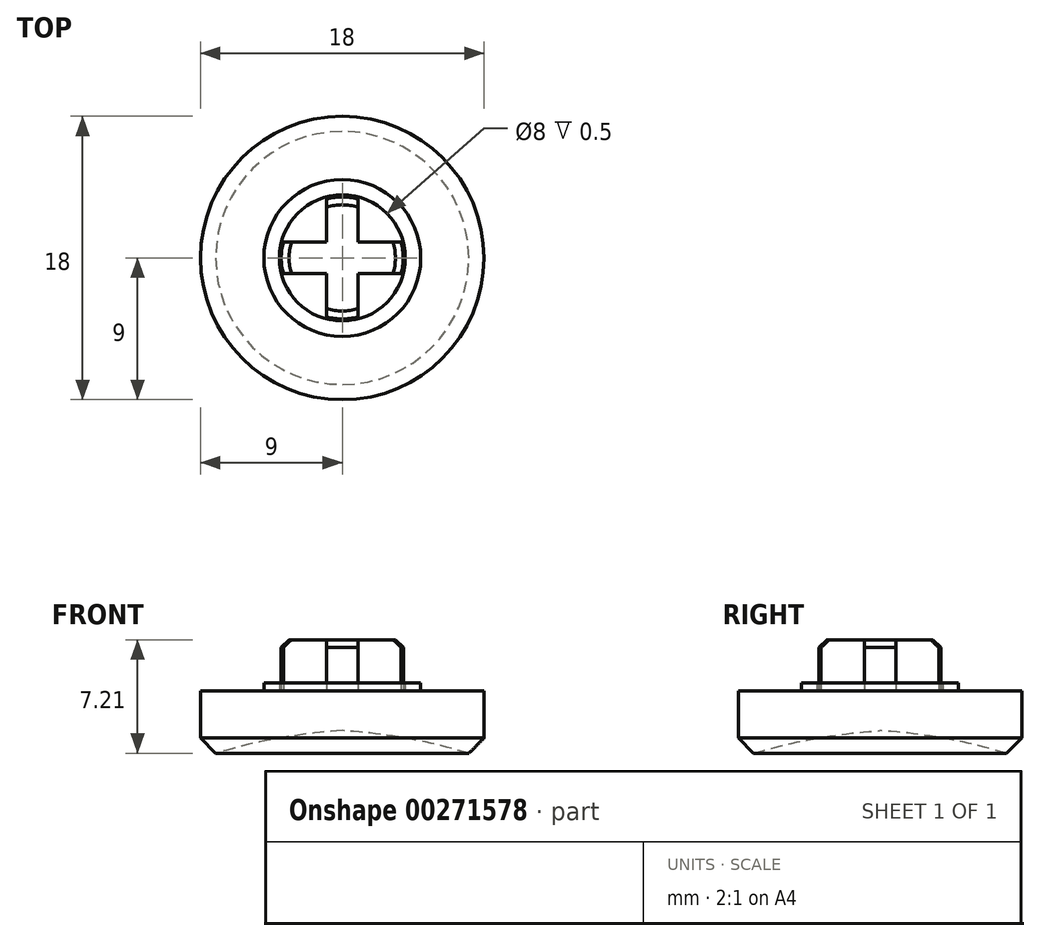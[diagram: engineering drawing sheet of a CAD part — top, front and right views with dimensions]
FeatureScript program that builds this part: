
annotation { "Feature Type Name" : "Feature", "Feature Type Description" : "" }
export const myFeature = defineFeature(function(context is Context, id is Id, definition is map)
    precondition{}
    {
        {
            var Q0;
            Q0=qCreatedBy(makeId("Top.planeOp"),FACE);
            var sketch = newSketch(context, id + "F0", { "sketchPlane" : qUnion([Q0])});
            skCircle(sketch, "E0", {"center": v(0, 0) * mm, "radius": 9 * mm});
            skLineSegment(sketch, "E1", {"start": v(-9.45, 0) * mm, "end": v(-9, 0) * mm});
            skLineSegment(sketch, "E2.left", {"start": v(-1, 3.74) * mm, "end": v(-1, 1) * mm});
            skLineSegment(sketch, "E2.right", {"start": v(1, 3.74) * mm, "end": v(1, 1) * mm});
            skLineSegment(sketch, "E3.bottom", {"start": v(-3.74, 1) * mm, "end": v(-1, 1) * mm});
            skLineSegment(sketch, "E3.top", {"start": v(-3.74, -1) * mm, "end": v(-1, -1) * mm});
            skCircle(sketch, "E4", {"center": v(0, 0) * mm, "radius": 3.88 * mm});
            skLineSegment(sketch, "E5.trimOffspring", {"start": v(1, 1) * mm, "end": v(3.74, 1) * mm});
            skLineSegment(sketch, "E6.trimOffspring", {"start": v(-1, -1) * mm, "end": v(-1, -3.74) * mm});
            skLineSegment(sketch, "E7.trimOffspring", {"start": v(1, -1) * mm, "end": v(1, -3.74) * mm});
            skLineSegment(sketch, "E8.trimOffspring", {"start": v(1, -1) * mm, "end": v(3.74, -1) * mm});
            skPoint(sketch, "E9.start.orphan", {"position": v(0, 9) * mm});
            skSolve(sketch);
        }
        {
            var Q0;
            Q0 = qSketchRegion(id + "F0", true);
            extrude(context, id + "F1", {"entities" : qUnion([Q0]), "depth" : 4 * mm});
        }
        {
            var Q0;
            Q0=makeQuery(id+"F1.opExtrude","CAP_FACE",FACE,{"disambiguationData":[OSD([sQuery(id+"F0.wireOp",EDGE,"E0")])],"isStart":false});
            var sketch = newSketch(context, id + "F2", { "sketchPlane" : qUnion([Q0])});
            skCircle(sketch, "E10", {"center": v(0, 0) * mm, "radius": 4 * mm});
            skCircle(sketch, "E11", {"center": v(0, 0) * mm, "radius": 4.98 * mm});
            skSolve(sketch);
        }
        {
            var Q0;
            {var subQ5=sQuery(id+"F0.wireOp",EDGE,"E2.left");Q0=makeQuery(id+"F0.imprint","IMPRINT",FACE,{"disambiguationData":[TD([[makeQuery(id+"F0.imprint","IMPRINT",EDGE,{"derivedFrom":subQ5}),1.0]])]});}
            extrude(context, id + "F3", {"entities" : qUnion([Q0]), "operationType" : NewBodyOperationType.ADD, "depth" : 7.25 * mm});
        }
        {
            var Q0;
            {var subQ0=sQuery(id+"F0.wireOp",EDGE,"E2.left");Q0=makeQuery(id+"F0.imprint","IMPRINT",FACE,{"disambiguationData":[TD([[makeQuery(id+"F0.imprint","IMPRINT",EDGE,{"derivedFrom":subQ0}),-1.0]])]});}
            var Q1;
            {var subQ0=sQuery(id+"F0.wireOp",EDGE,"E2.right");Q1=makeQuery(id+"F0.imprint","IMPRINT",FACE,{"disambiguationData":[TD([[makeQuery(id+"F0.imprint","IMPRINT",EDGE,{"derivedFrom":subQ0}),1.0]])]});}
            var Q2;
            {var subQ0=sQuery(id+"F0.wireOp",EDGE,"E7.trimOffspring");Q2=makeQuery(id+"F0.imprint","IMPRINT",FACE,{"disambiguationData":[TD([[makeQuery(id+"F0.imprint","IMPRINT",EDGE,{"derivedFrom":subQ0}),1.0]])]});}
            var Q3;
            {var subQ0=sQuery(id+"F0.wireOp",EDGE,"E3.top");Q3=makeQuery(id+"F0.imprint","IMPRINT",FACE,{"disambiguationData":[TD([[makeQuery(id+"F0.imprint","IMPRINT",EDGE,{"derivedFrom":subQ0}),-1.0]])]});}
            extrude(context, id + "F4", {"entities" : qUnion([Q0, Q1, Q2, Q3]), "operationType" : NewBodyOperationType.ADD, "depth" : 4 * mm});
        }
        {
            var Q0;
            {var subQ0=sQuery(id+"F0.wireOp",EDGE,"E4");Q0=makeQuery(id+"F3.opExtrude","CAP_EDGE",EDGE,{"disambiguationData":[OSD([subQ0]),TDD([makeQuery(id+"F0.imprint","IMPRINT",EDGE,{"disambiguationData":[TD([[makeQuery(id+"F0.imprint","INTERSECT",VERTEX,{"derivedFrom":[sQuery(id+"F0.wireOp",EDGE,"E3.bottom"),subQ0]}),-1.0]])],"derivedFrom":subQ0})])],"isStart":false});}
            var Q1;
            {var subQ0=sQuery(id+"F0.wireOp",EDGE,"E4");Q1=makeQuery(id+"F3.opExtrude","CAP_EDGE",EDGE,{"disambiguationData":[OSD([subQ0]),TDD([makeQuery(id+"F0.imprint","IMPRINT",EDGE,{"disambiguationData":[TD([[makeQuery(id+"F0.imprint","INTERSECT",VERTEX,{"derivedFrom":[sQuery(id+"F0.wireOp",EDGE,"E2.left"),subQ0]}),1.0]])],"derivedFrom":subQ0})])],"isStart":false});}
            var Q2;
            {var subQ0=sQuery(id+"F0.wireOp",EDGE,"E4");Q2=makeQuery(id+"F3.opExtrude","CAP_EDGE",EDGE,{"disambiguationData":[OSD([subQ0]),TDD([makeQuery(id+"F0.imprint","IMPRINT",EDGE,{"disambiguationData":[TD([[makeQuery(id+"F0.imprint","INTERSECT",VERTEX,{"derivedFrom":[subQ0,sQuery(id+"F0.wireOp",EDGE,"E5.trimOffspring")]}),1.0]])],"derivedFrom":subQ0})])],"isStart":false});}
            var Q3;
            {var subQ0=sQuery(id+"F0.wireOp",EDGE,"E4");Q3=makeQuery(id+"F3.opExtrude","CAP_EDGE",EDGE,{"disambiguationData":[OSD([subQ0]),TDD([makeQuery(id+"F0.imprint","IMPRINT",EDGE,{"disambiguationData":[TD([[makeQuery(id+"F0.imprint","INTERSECT",VERTEX,{"derivedFrom":[subQ0,sQuery(id+"F0.wireOp",EDGE,"E6.trimOffspring")]}),-1.0]])],"derivedFrom":subQ0})])],"isStart":false});}
            chamfer(context, id + "F5", {"entities" : qUnion([Q0, Q1, Q2, Q3]), "width" : 0.5 * mm, "tangentPropagation" : true});
        }
        {
            var Q0;
            {var subQ0=sQuery(id+"F0.wireOp",EDGE,"E8.trimOffspring");var subQ1=sQuery(id+"F0.wireOp",EDGE,"E7.trimOffspring");var subQ2=sQuery(id+"F0.wireOp",EDGE,"E4");var subQ3=sQuery(id+"F0.wireOp",EDGE,"E6.trimOffspring");var subQ4=sQuery(id+"F0.wireOp",EDGE,"E3.top");var subQ5=sQuery(id+"F0.wireOp",EDGE,"E5.trimOffspring");var subQ6=sQuery(id+"F0.wireOp",EDGE,"E2.right");var subQ7=sQuery(id+"F0.wireOp",EDGE,"E3.bottom");var subQ8=sQuery(id+"F0.wireOp",EDGE,"E2.left");Q0=makeQuery(id+"F4.boolean.opBoolean","MERGE",FACE,{"derivedFrom":[makeQuery(id+"F3.boolean.opBoolean","MERGE",FACE,{"derivedFrom":[makeQuery(id+"F1.opExtrude","CAP_FACE",FACE,{"disambiguationData":[OSD([sQuery(id+"F0.wireOp",EDGE,"E0"),subQ2])],"isStart":true}),makeQuery(id+"F3.opExtrude","CAP_FACE",FACE,{"disambiguationData":[OSD([subQ8,subQ6,subQ7,subQ4,subQ2,subQ5,subQ3,subQ1,subQ0])],"isStart":true})]}),makeQuery(id+"F4.opExtrude","CAP_FACE",FACE,{"disambiguationData":[OSD([subQ8,subQ7,subQ2])],"isStart":true}),makeQuery(id+"F4.opExtrude","CAP_FACE",FACE,{"disambiguationData":[OSD([subQ6,subQ2,subQ5])],"isStart":true}),makeQuery(id+"F4.opExtrude","CAP_FACE",FACE,{"disambiguationData":[OSD([subQ4,subQ2,subQ3])],"isStart":true}),makeQuery(id+"F4.opExtrude","CAP_FACE",FACE,{"disambiguationData":[OSD([subQ2,subQ1,subQ0])],"isStart":true})]});}
            chamfer(context, id + "F6", {"entities" : qUnion([Q0]), "width" : 1 * mm, "tangentPropagation" : true});
        }
        {
            var Q0;
            Q0=qCreatedBy(makeId("Right.planeOp"),FACE);
            var sketch = newSketch(context, id + "F7", { "sketchPlane" : qUnion([Q0])});
            skLineSegment(sketch, "E12", {"start": v(0, 0) * mm, "end": v(0, 1.48) * mm});
            skLineSegment(sketch, "E13", {"start": v(0, 0) * mm, "end": v(8.16, 0) * mm});
            skArc(sketch, "E14", {"start": v(8.16, 0) * mm, "mid": v(4.12, 0.98) * mm, "end": v(0, 1.48) * mm});
            skLineSegment(sketch, "E15", {"start": v(0, -0.97) * mm, "end": v(0, 1.81) * mm, "construction": true});
            skSolve(sketch);
        }
        {
            var Q0;
            Q0=makeQuery(id+"F7.imprint","IMPRINT",FACE,{"disambiguationData":[TD([[makeQuery(id+"F7.imprint","IMPRINT",EDGE,{"derivedFrom":sQuery(id+"F7.wireOp",EDGE,"E12")}),-1.0]])]});
            var Q1;
            Q1=sQuery(id+"F7.wireOp",EDGE,"E15");
            revolve(context, id + "F8", {"operationType" : NewBodyOperationType.REMOVE, "entities" : qUnion([Q0]), "axis" : qUnion([Q1]), "revolveType" : RevolveType.FULL, "oppositeDirection" : true});
        }
        {
            var Q0;
            Q0 = qSketchRegion(id + "F2", true);
            extrude(context, id + "F9", {"entities" : qUnion([Q0]), "operationType" : NewBodyOperationType.ADD, "depth" : .5 * mm});
        }
    });
